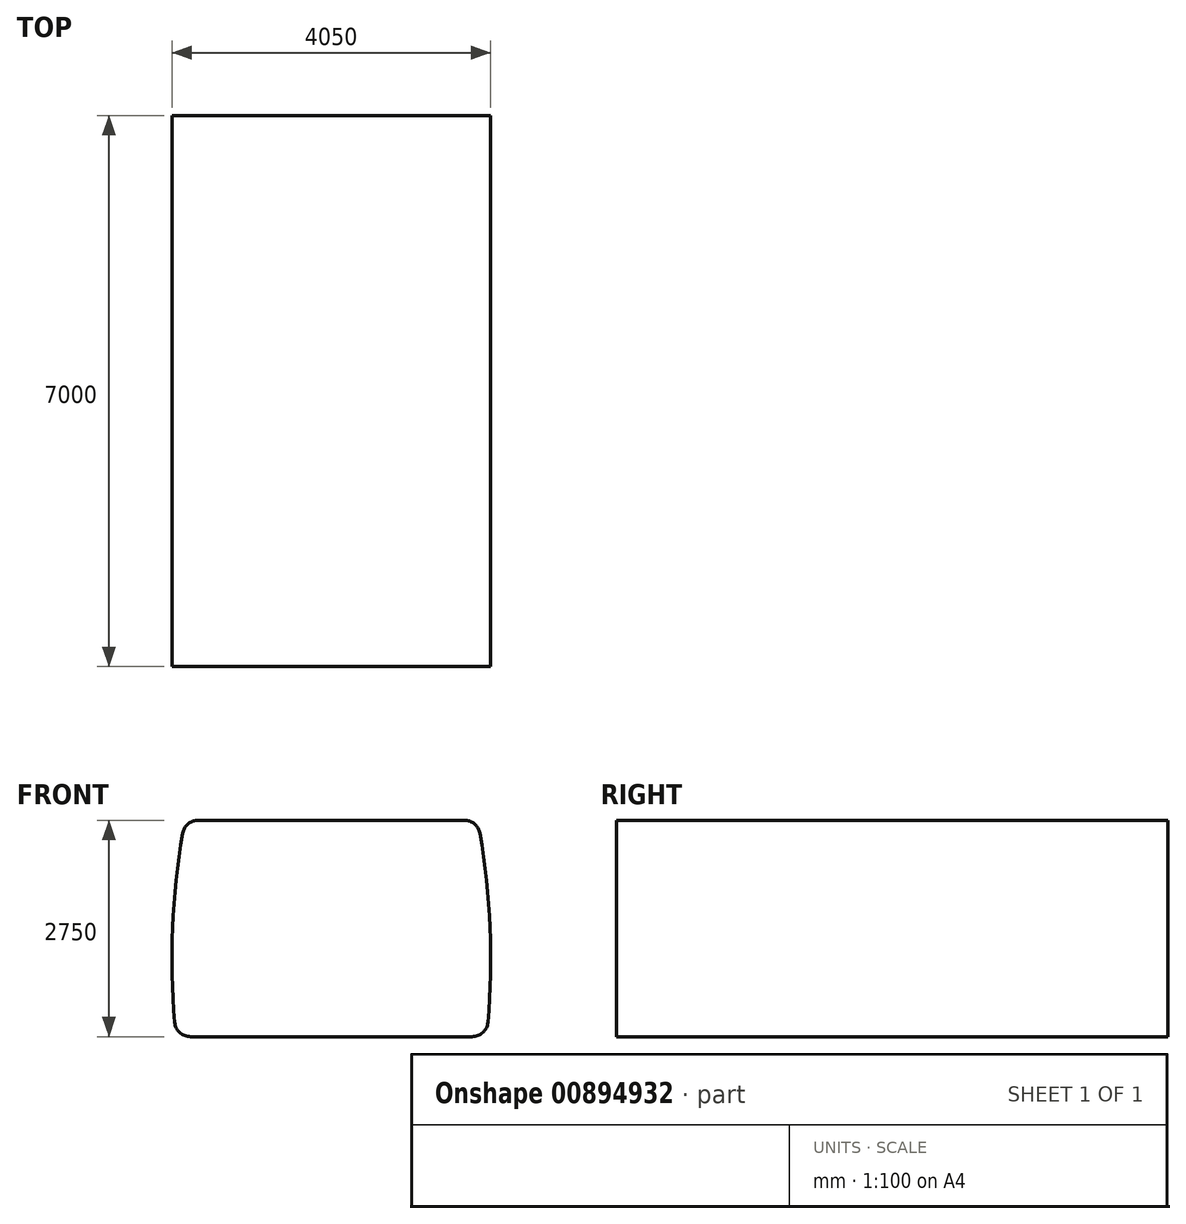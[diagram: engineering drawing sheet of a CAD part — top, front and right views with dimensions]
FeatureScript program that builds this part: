
annotation { "Feature Type Name" : "Feature", "Feature Type Description" : "" }
export const myFeature = defineFeature(function(context is Context, id is Id, definition is map)
    precondition{}
    {
        {
            var Q0;
            Q0=qCreatedBy(makeId("Front.planeOp"),FACE);
            var sketch = newSketch(context, id + "F0", { "sketchPlane" : qUnion([Q0])});
            skLineSegment(sketch, "E0.bottom", {"start": v(-1790, -1375) * mm, "end": v(0, -1375) * mm});
            skLineSegment(sketch, "E0.top", {"start": v(-1690.46, 1375) * mm, "end": v(0, 1375) * mm});
            skLineSegment(sketch, "E0.left", {"start": v(-2025, -1500) * mm, "end": v(-2025, 1500) * mm, "construction": true});
            skPoint(sketch, "E0.middle", {"position": v(0, 0) * mm});
            skArc(sketch, "E1", {"start": v(-1887.5, 1209.35) * mm, "mid": v(-2016.71, 11.71) * mm, "end": v(-1989.23, -1192.57) * mm});
            skPoint(sketch, "E2.newPointA", {"position": v(-2062.5, 1375) * mm});
            skArc(sketch, "E2.filletArc", {"start": v(-1690.46, 1375) * mm, "mid": v(-1819.17, 1328.09) * mm, "end": v(-1887.5, 1209.35) * mm});
            skPoint(sketch, "E3.newPointB", {"position": v(-2062.5, -1375) * mm});
            skArc(sketch, "E3.filletArc", {"start": v(-1989.23, -1192.57) * mm, "mid": v(-1925.07, -1322.5) * mm, "end": v(-1790, -1375) * mm});
            skLineSegment(sketch, "E4", {"start": v(0, 1910.43) * mm, "end": v(0, -2514) * mm, "construction": true});
            skPoint(sketch, "E0.right.end.orphan", {"position": v(2062.5, 1375) * mm});
            skPoint(sketch, "E5.orphan", {"position": v(2062.5, -1375) * mm});
            skLineSegment(sketch, "E6.MirrorCS", {"start": v(1690.46, 1375) * mm, "end": v(0, 1375) * mm});
            skArc(sketch, "E7.MirrorCS", {"start": v(1690.46, 1375) * mm, "mid": v(1819.17, 1328.09) * mm, "end": v(1887.5, 1209.35) * mm});
            skArc(sketch, "E8.MirrorCS", {"start": v(1887.5, 1209.35) * mm, "mid": v(2016.71, 11.71) * mm, "end": v(1989.23, -1192.57) * mm});
            skLineSegment(sketch, "E9.MirrorCS", {"start": v(1790, -1375) * mm, "end": v(0, -1375) * mm});
            skArc(sketch, "E10.MirrorCS", {"start": v(1989.23, -1192.57) * mm, "mid": v(1925.07, -1322.5) * mm, "end": v(1790, -1375) * mm});
            skSolve(sketch);
        }
        {
            var Q0;
            Q0=makeQuery(id+"F0.imprint","IMPRINT",FACE,{"disambiguationData":[TD([[makeQuery(id+"F0.imprint","IMPRINT",EDGE,{"derivedFrom":sQuery(id+"F0.wireOp",EDGE,"E0.bottom")}),1.0]])]});
            extrude(context, id + "F1", {"entities" : qUnion([Q0]), "depth" : 7000 * mm, "offsetDistance" : 25 * mm});
        }
    });
